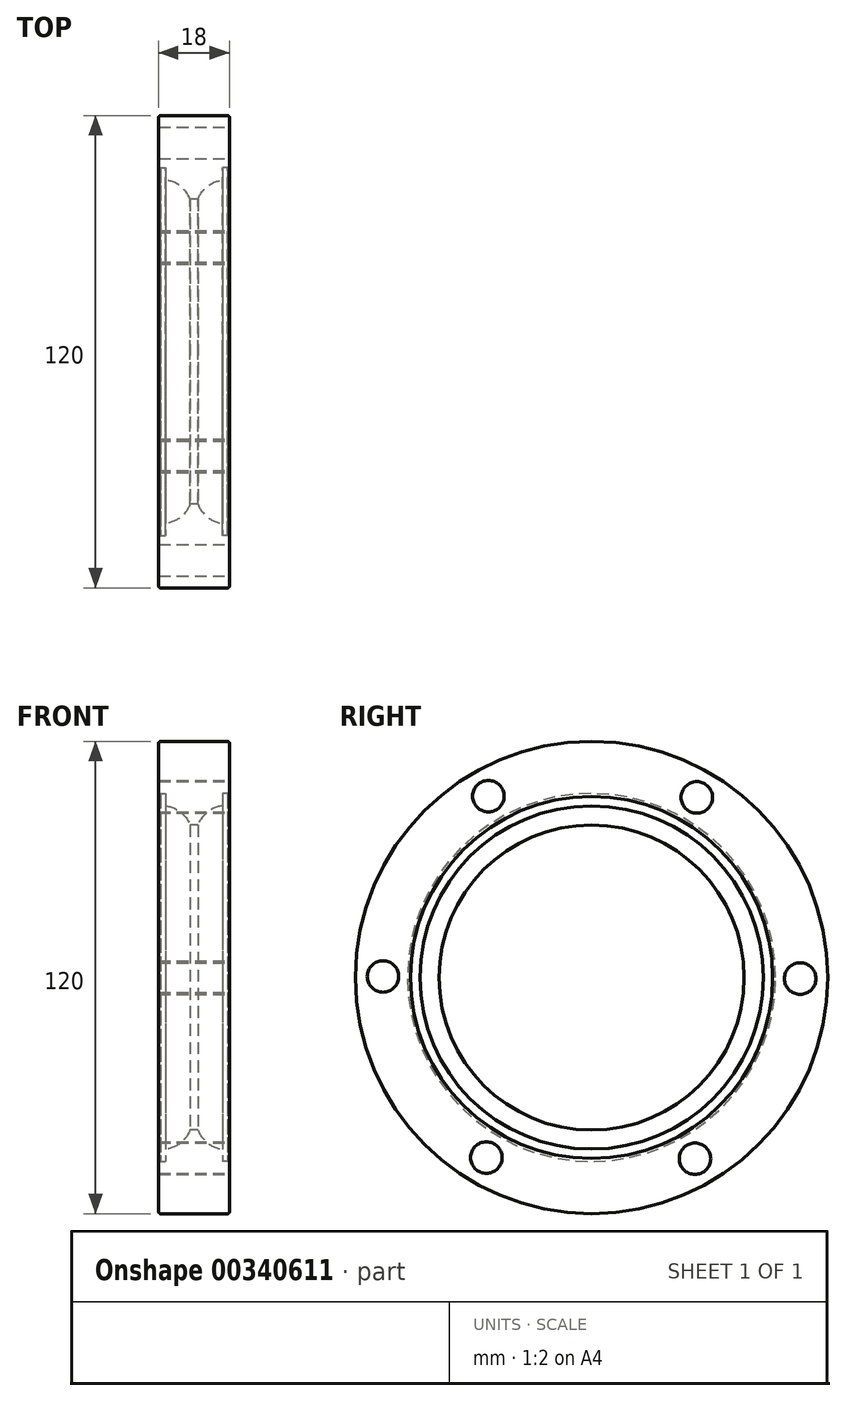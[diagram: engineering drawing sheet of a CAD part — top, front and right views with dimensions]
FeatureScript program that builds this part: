
annotation { "Feature Type Name" : "Feature", "Feature Type Description" : "" }
export const myFeature = defineFeature(function(context is Context, id is Id, definition is map)
    precondition{}
    {
        {
            var Q0;
            Q0=qCreatedBy(makeId("Front.planeOp"),FACE);
            var sketch = newSketch(context, id + "F0", { "sketchPlane" : qUnion([Q0])});
            skLineSegment(sketch, "E0", {"start": v(0, 60) * mm, "end": v(9, 60) * mm});
            skLineSegment(sketch, "E1", {"start": v(0, 60) * mm, "end": v(0, 38.75) * mm});
            skLineSegment(sketch, "E2", {"start": v(0, 38.75) * mm, "end": v(1, 38.75) * mm});
            skLineSegment(sketch, "E3", {"start": v(9, 60) * mm, "end": v(9, 46) * mm});
            skLineSegment(sketch, "E4", {"start": v(9, 46) * mm, "end": v(8.5, 46) * mm});
            skLineSegment(sketch, "E5", {"start": v(7.2, 43.6) * mm, "end": v(7.2, 46) * mm});
            skPoint(sketch, "E5.endSnap0", {"position": v(8.75, 46) * mm});
            skLineSegment(sketch, "E6", {"start": v(7.2, 46) * mm, "end": v(7.2, 46.75) * mm});
            skLineSegment(sketch, "E7", {"start": v(8.5, 46.75) * mm, "end": v(7.2, 46.75) * mm});
            skLineSegment(sketch, "E8", {"start": v(8.5, 46.75) * mm, "end": v(8.5, 46) * mm});
            skArc(sketch, "E9", {"start": v(7.2, 43.6) * mm, "mid": v(3.42, 42.04) * mm, "end": v(1, 38.75) * mm});
            skLineSegment(sketch, "E10", {"start": v(0, 0) * mm, "end": v(26.4, 0) * mm});
            skSolve(sketch);
        }
        {
            var Q0;
            Q0=makeQuery(id+"F0.imprint","IMPRINT",FACE,{"disambiguationData":[TD([[makeQuery(id+"F0.imprint","IMPRINT",EDGE,{"derivedFrom":sQuery(id+"F0.wireOp",EDGE,"E0")}),-1.0]])]});
            var Q1;
            Q1=sQuery(id+"F0.wireOp",EDGE,"E10");
            revolve(context, id + "F1", {"entities" : qUnion([Q0]), "axis" : qUnion([Q1]), "revolveType" : RevolveType.FULL});
        }
        {
            var Q0;
            Q0=makeQuery(id+"Ffd5v97EGCt3Kdj_1.opPattern","COPY",EDGE,{"derivedFrom":makeQuery(id+"F1.opRevolve","SWEPT_EDGE",EDGE,{"disambiguationData":[OSD([sQuery(id+"F0.wireOp",EDGE,"E0"),sQuery(id+"F0.wireOp",EDGE,"E3")])]}),"instanceName":"1"});
            var Q1;
            Q1=makeQuery(id+"F1.opRevolve","SWEPT_EDGE",EDGE,{"disambiguationData":[OSD([sQuery(id+"F0.wireOp",EDGE,"E0"),sQuery(id+"F0.wireOp",EDGE,"E3")])]});
            fillet(context, id + "F2", {"entities" : qUnion([Q0, Q1]), "radius" : 0.5 * mm, "tangentPropagation" : true, "allowEdgeOverflow" : false});
        }
        {
            var Q0;
            Q0=makeQuery(id+"F1.opRevolve","SWEPT_BODY",BODY,{"disambiguationData":[OSD([sQuery(id+"F0.wireOp",EDGE,"E0"),sQuery(id+"F0.wireOp",EDGE,"E1"),sQuery(id+"F0.wireOp",EDGE,"E2"),sQuery(id+"F0.wireOp",EDGE,"E3"),sQuery(id+"F0.wireOp",EDGE,"E4"),sQuery(id+"F0.wireOp",EDGE,"E5"),sQuery(id+"F0.wireOp",EDGE,"E6"),sQuery(id+"F0.wireOp",EDGE,"E7"),sQuery(id+"F0.wireOp",EDGE,"E8"),sQuery(id+"F0.wireOp",EDGE,"E9")])]});
            var Q1;
            Q1=makeQuery(id+"F1.opRevolve","SWEPT_FACE",FACE,{"disambiguationData":[OSD([sQuery(id+"F0.wireOp",EDGE,"E1")])]});
            mirror(context, id + "F3", {"operationType" : NewBodyOperationType.ADD, "entities" : qUnion([Q0]), "mirrorPlane" : qUnion([Q1])});
        }
        {
            var Q0;
            Q0=makeQuery(id+"F1.opRevolve","SWEPT_FACE",FACE,{"disambiguationData":[OSD([sQuery(id+"F0.wireOp",EDGE,"E3")])]});
            var sketch = newSketch(context, id + "F4", { "sketchPlane" : qUnion([Q0])});
            skCircle(sketch, "E11", {"center": v(-26.22, 46.06) * mm, "radius": 4 * mm});
            skPoint(sketch, "E12.0.midPoint", {"position": v(-39.63, 23.15) * mm});
            skCircle(sketch, "E13", {"center": v(26.74, 45.76) * mm, "radius": 4 * mm});
            skCircle(sketch, "E14", {"center": v(53, -0.28) * mm, "radius": 4 * mm});
            skCircle(sketch, "E15", {"center": v(26.26, -46.04) * mm, "radius": 4 * mm});
            skCircle(sketch, "E16", {"center": v(-26.74, -45.76) * mm, "radius": 4 * mm});
            skCircle(sketch, "E17", {"center": v(-53, 0.28) * mm, "radius": 4 * mm});
            skSolve(sketch);
        }
        {
            var Q0;
            Q0=makeQuery(id+"F4.imprint","IMPRINT",FACE,{"disambiguationData":[TD([[makeQuery(id+"F4.imprint","IMPRINT",EDGE,{"derivedFrom":sQuery(id+"F4.wireOp",EDGE,"E17")}),1.0]])]});
            var Q1;
            Q1=makeQuery(id+"F4.imprint","IMPRINT",FACE,{"disambiguationData":[TD([[makeQuery(id+"F4.imprint","IMPRINT",EDGE,{"derivedFrom":sQuery(id+"F4.wireOp",EDGE,"E11")}),1.0]])]});
            var Q2;
            Q2=makeQuery(id+"F4.imprint","IMPRINT",FACE,{"disambiguationData":[TD([[makeQuery(id+"F4.imprint","IMPRINT",EDGE,{"derivedFrom":sQuery(id+"F4.wireOp",EDGE,"E13")}),1.0]])]});
            var Q3;
            Q3=makeQuery(id+"F4.imprint","IMPRINT",FACE,{"disambiguationData":[TD([[makeQuery(id+"F4.imprint","IMPRINT",EDGE,{"derivedFrom":sQuery(id+"F4.wireOp",EDGE,"E14")}),1.0]])]});
            var Q4;
            Q4=makeQuery(id+"F4.imprint","IMPRINT",FACE,{"disambiguationData":[TD([[makeQuery(id+"F4.imprint","IMPRINT",EDGE,{"derivedFrom":sQuery(id+"F4.wireOp",EDGE,"E15")}),1.0]])]});
            var Q5;
            Q5=makeQuery(id+"F4.imprint","IMPRINT",FACE,{"disambiguationData":[TD([[makeQuery(id+"F4.imprint","IMPRINT",EDGE,{"derivedFrom":sQuery(id+"F4.wireOp",EDGE,"E16")}),1.0]])]});
            extrude(context, id + "F5", {"entities" : qUnion([Q0, Q1, Q2, Q3, Q4, Q5]), "operationType" : NewBodyOperationType.REMOVE, "oppositeDirection" : true, "depth" : 18 * mm});
        }
    });
